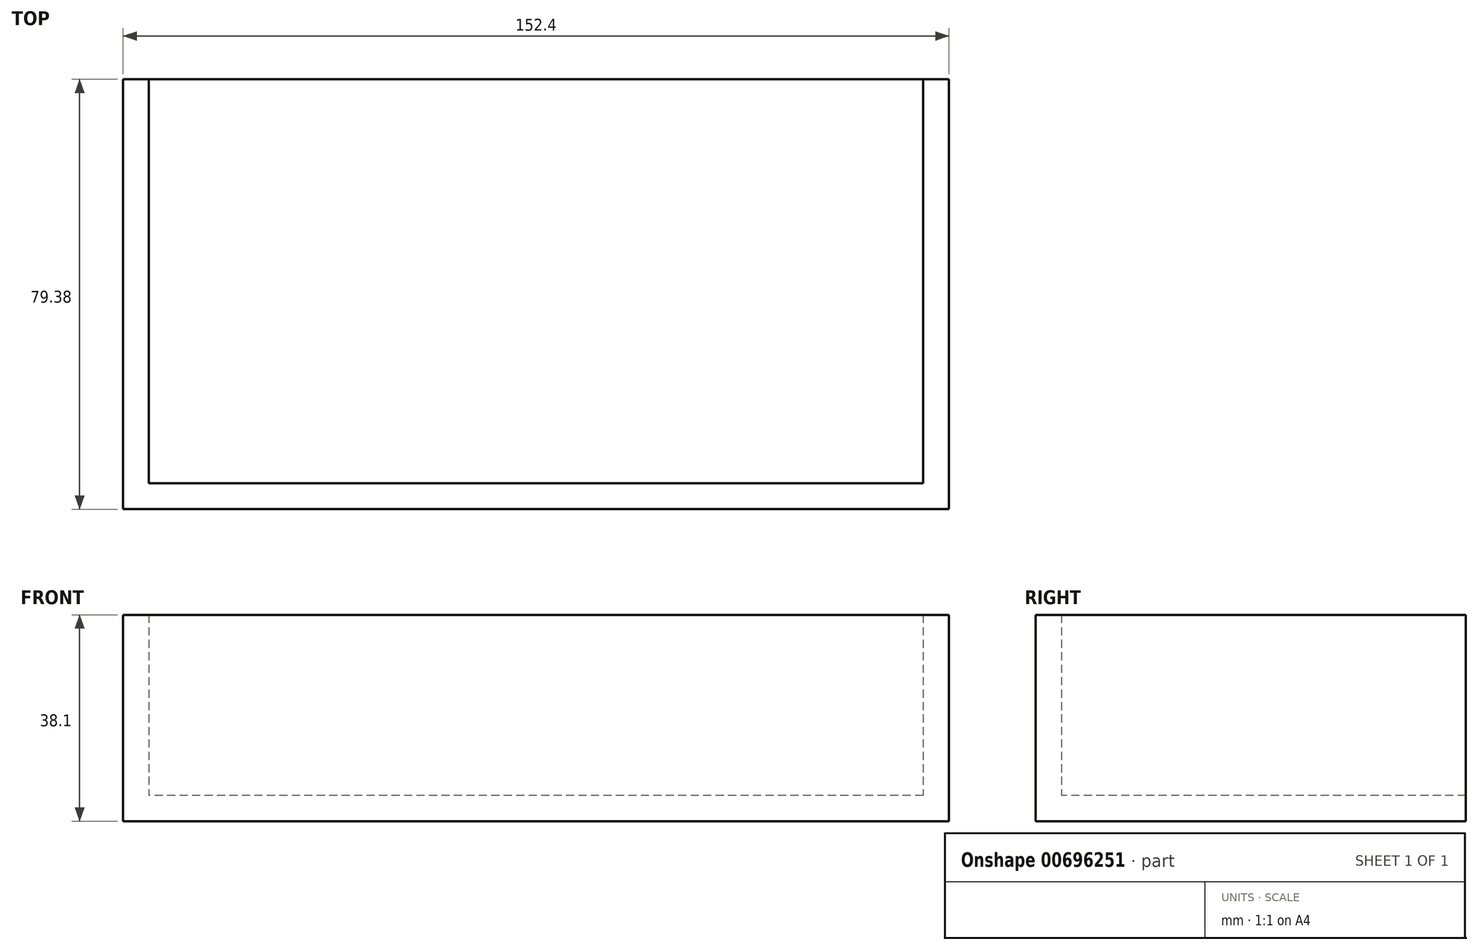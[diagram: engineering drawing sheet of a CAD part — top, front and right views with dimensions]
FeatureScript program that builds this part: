
annotation { "Feature Type Name" : "Feature", "Feature Type Description" : "" }
export const myFeature = defineFeature(function(context is Context, id is Id, definition is map)
    precondition{}
    {
        {
            var Q0;
            Q0=qCreatedBy(makeId("Top.planeOp"),FACE);
            var sketch = newSketch(context, id + "F0", { "sketchPlane" : qUnion([Q0])});
            skLineSegment(sketch, "E0.bottom", {"start": v(76.2, 39.69) * mm, "end": v(-76.2, 39.69) * mm});
            skLineSegment(sketch, "E0.top", {"start": v(76.2, -39.69) * mm, "end": v(-76.2, -39.69) * mm});
            skLineSegment(sketch, "E0.left", {"start": v(76.2, 39.69) * mm, "end": v(76.2, -39.69) * mm});
            skLineSegment(sketch, "E0.right", {"start": v(-76.2, 39.69) * mm, "end": v(-76.2, -39.69) * mm});
            skPoint(sketch, "E0.middle", {"position": v(0, 0) * mm});
            skPoint(sketch, "E1.visualSharp", {"position": v(-76.2, 39.69) * mm});
            skPoint(sketch, "E2.visualSharp", {"position": v(-76.2, -39.69) * mm});
            skPoint(sketch, "E3.visualSharp", {"position": v(76.2, -39.69) * mm});
            skPoint(sketch, "E4.visualSharp", {"position": v(76.2, 39.69) * mm});
            skSolve(sketch);
        }
        {
            var Q0;
            Q0 = qSketchRegion(id + "F0", true);
            extrude(context, id + "F1", {"entities" : qUnion([Q0]), "depth" : 38.1 * mm, "offsetDistance" : 25.4 * mm});
        }
        {
            var Q0;
            Q0=makeQuery(id+"F1.opExtrude","CAP_FACE",FACE,{"disambiguationData":[OSD([sQuery(id+"F0.wireOp",EDGE,"E0.bottom"),sQuery(id+"F0.wireOp",EDGE,"E0.top"),sQuery(id+"F0.wireOp",EDGE,"E0.left"),sQuery(id+"F0.wireOp",EDGE,"E0.right")])],"isStart":false});
            var Q1;
            Q1=makeQuery(id+"F1.opExtrude","SWEPT_FACE",FACE,{"disambiguationData":[OSD([sQuery(id+"F0.wireOp",EDGE,"E0.bottom")])]});
            shell(context, id + "F2", {"entities" : qUnion([Q0, Q1]), "thickness" : 4.76 * mm});
        }
    });
